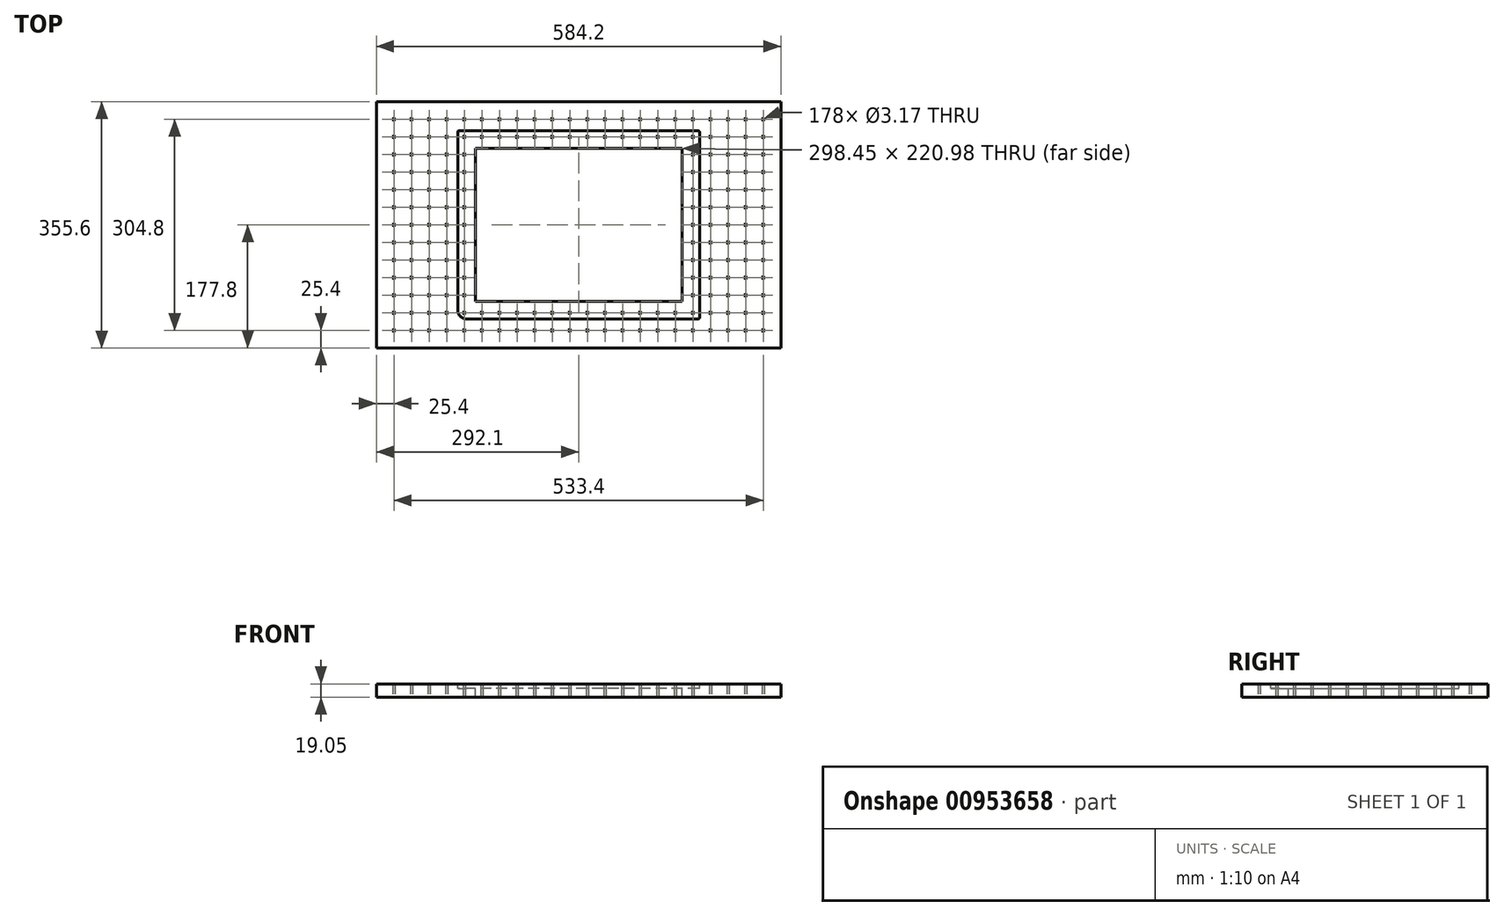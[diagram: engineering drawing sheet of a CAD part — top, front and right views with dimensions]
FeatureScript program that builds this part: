
annotation { "Feature Type Name" : "Feature", "Feature Type Description" : "" }
export const myFeature = defineFeature(function(context is Context, id is Id, definition is map)
    precondition{}
    {
        {
            var Q0;
            Q0=qCreatedBy(makeId("Top.planeOp"),FACE);
            var sketch = newSketch(context, id + "F0", { "sketchPlane" : qUnion([Q0])});
            skLineSegment(sketch, "E0.bottom", {"start": v(292.1, -177.8) * mm, "end": v(-292.1, -177.8) * mm});
            skLineSegment(sketch, "E0.top", {"start": v(292.1, 177.8) * mm, "end": v(-292.1, 177.8) * mm});
            skLineSegment(sketch, "E0.left", {"start": v(292.1, -177.8) * mm, "end": v(292.1, 177.8) * mm});
            skLineSegment(sketch, "E0.right", {"start": v(-292.1, -177.8) * mm, "end": v(-292.1, 177.8) * mm});
            skLineSegment(sketch, "E1", {"start": v(-292.1, -177.8) * mm, "end": v(-292.1, -152.4) * mm, "construction": true});
            skLineSegment(sketch, "E2", {"start": v(-292.1, -152.4) * mm, "end": v(-266.7, -152.4) * mm, "construction": true});
            skCircle(sketch, "E3", {"center": v(-266.7, -152.4) * mm, "radius": 1.59 * mm});
            skCircle(sketch, "E4.0.1.0", {"center": v(-266.7, -127) * mm, "radius": 1.59 * mm});
            skCircle(sketch, "E4.0.2.0", {"center": v(-266.7, -101.6) * mm, "radius": 1.59 * mm});
            skCircle(sketch, "E4.0.3.0", {"center": v(-266.7, -76.2) * mm, "radius": 1.59 * mm});
            skCircle(sketch, "E4.0.4.0", {"center": v(-266.7, -50.8) * mm, "radius": 1.59 * mm});
            skCircle(sketch, "E4.0.5.0", {"center": v(-266.7, -25.4) * mm, "radius": 1.59 * mm});
            skCircle(sketch, "E4.0.6.0", {"center": v(-266.7, 0) * mm, "radius": 1.59 * mm});
            skCircle(sketch, "E4.0.7.0", {"center": v(-266.7, 25.4) * mm, "radius": 1.59 * mm});
            skCircle(sketch, "E4.0.8.0", {"center": v(-266.7, 50.8) * mm, "radius": 1.59 * mm});
            skCircle(sketch, "E4.0.9.0", {"center": v(-266.7, 76.2) * mm, "radius": 1.59 * mm});
            skCircle(sketch, "E4.0.10.0", {"center": v(-266.7, 101.6) * mm, "radius": 1.59 * mm});
            skCircle(sketch, "E4.0.11.0", {"center": v(-266.7, 127) * mm, "radius": 1.59 * mm});
            skCircle(sketch, "E4.0.12.0", {"center": v(-266.7, 152.4) * mm, "radius": 1.59 * mm});
            skCircle(sketch, "E4.1.0.0", {"center": v(-241.3, -152.4) * mm, "radius": 1.59 * mm});
            skCircle(sketch, "E4.1.1.0", {"center": v(-241.3, -127) * mm, "radius": 1.59 * mm});
            skCircle(sketch, "E4.1.2.0", {"center": v(-241.3, -101.6) * mm, "radius": 1.59 * mm});
            skCircle(sketch, "E4.1.3.0", {"center": v(-241.3, -76.2) * mm, "radius": 1.59 * mm});
            skCircle(sketch, "E4.1.4.0", {"center": v(-241.3, -50.8) * mm, "radius": 1.59 * mm});
            skCircle(sketch, "E4.1.5.0", {"center": v(-241.3, -25.4) * mm, "radius": 1.59 * mm});
            skCircle(sketch, "E4.1.6.0", {"center": v(-241.3, 0) * mm, "radius": 1.59 * mm});
            skCircle(sketch, "E4.1.7.0", {"center": v(-241.3, 25.4) * mm, "radius": 1.59 * mm});
            skCircle(sketch, "E4.1.8.0", {"center": v(-241.3, 50.8) * mm, "radius": 1.59 * mm});
            skCircle(sketch, "E4.1.9.0", {"center": v(-241.3, 76.2) * mm, "radius": 1.59 * mm});
            skCircle(sketch, "E4.1.10.0", {"center": v(-241.3, 101.6) * mm, "radius": 1.59 * mm});
            skCircle(sketch, "E4.1.11.0", {"center": v(-241.3, 127) * mm, "radius": 1.59 * mm});
            skCircle(sketch, "E4.1.12.0", {"center": v(-241.3, 152.4) * mm, "radius": 1.59 * mm});
            skCircle(sketch, "E4.2.0.0", {"center": v(-215.9, -152.4) * mm, "radius": 1.59 * mm});
            skCircle(sketch, "E4.2.1.0", {"center": v(-215.9, -127) * mm, "radius": 1.59 * mm});
            skCircle(sketch, "E4.2.2.0", {"center": v(-215.9, -101.6) * mm, "radius": 1.59 * mm});
            skCircle(sketch, "E4.2.3.0", {"center": v(-215.9, -76.2) * mm, "radius": 1.59 * mm});
            skCircle(sketch, "E4.2.4.0", {"center": v(-215.9, -50.8) * mm, "radius": 1.59 * mm});
            skCircle(sketch, "E4.2.5.0", {"center": v(-215.9, -25.4) * mm, "radius": 1.59 * mm});
            skCircle(sketch, "E4.2.6.0", {"center": v(-215.9, 0) * mm, "radius": 1.59 * mm});
            skCircle(sketch, "E4.2.7.0", {"center": v(-215.9, 25.4) * mm, "radius": 1.59 * mm});
            skCircle(sketch, "E4.2.8.0", {"center": v(-215.9, 50.8) * mm, "radius": 1.59 * mm});
            skCircle(sketch, "E4.2.9.0", {"center": v(-215.9, 76.2) * mm, "radius": 1.59 * mm});
            skCircle(sketch, "E4.2.10.0", {"center": v(-215.9, 101.6) * mm, "radius": 1.59 * mm});
            skCircle(sketch, "E4.2.11.0", {"center": v(-215.9, 127) * mm, "radius": 1.59 * mm});
            skCircle(sketch, "E4.2.12.0", {"center": v(-215.9, 152.4) * mm, "radius": 1.59 * mm});
            skCircle(sketch, "E4.3.0.0", {"center": v(-190.5, -152.4) * mm, "radius": 1.59 * mm});
            skCircle(sketch, "E4.3.1.0", {"center": v(-190.5, -127) * mm, "radius": 1.59 * mm});
            skCircle(sketch, "E4.3.2.0", {"center": v(-190.5, -101.6) * mm, "radius": 1.59 * mm});
            skCircle(sketch, "E4.3.3.0", {"center": v(-190.5, -76.2) * mm, "radius": 1.59 * mm});
            skCircle(sketch, "E4.3.4.0", {"center": v(-190.5, -50.8) * mm, "radius": 1.59 * mm});
            skCircle(sketch, "E4.3.5.0", {"center": v(-190.5, -25.4) * mm, "radius": 1.59 * mm});
            skCircle(sketch, "E4.3.6.0", {"center": v(-190.5, 0) * mm, "radius": 1.59 * mm});
            skCircle(sketch, "E4.3.7.0", {"center": v(-190.5, 25.4) * mm, "radius": 1.59 * mm});
            skCircle(sketch, "E4.3.8.0", {"center": v(-190.5, 50.8) * mm, "radius": 1.59 * mm});
            skCircle(sketch, "E4.3.9.0", {"center": v(-190.5, 76.2) * mm, "radius": 1.59 * mm});
            skCircle(sketch, "E4.3.10.0", {"center": v(-190.5, 101.6) * mm, "radius": 1.59 * mm});
            skCircle(sketch, "E4.3.11.0", {"center": v(-190.5, 127) * mm, "radius": 1.59 * mm});
            skCircle(sketch, "E4.3.12.0", {"center": v(-190.5, 152.4) * mm, "radius": 1.59 * mm});
            skCircle(sketch, "E4.4.0.0", {"center": v(-165.1, -152.4) * mm, "radius": 1.59 * mm});
            skCircle(sketch, "E4.4.1.0", {"center": v(-165.1, -127) * mm, "radius": 1.59 * mm});
            skCircle(sketch, "E4.4.2.0", {"center": v(-165.1, -101.6) * mm, "radius": 1.59 * mm});
            skCircle(sketch, "E4.4.3.0", {"center": v(-165.1, -76.2) * mm, "radius": 1.59 * mm});
            skCircle(sketch, "E4.4.4.0", {"center": v(-165.1, -50.8) * mm, "radius": 1.59 * mm});
            skCircle(sketch, "E4.4.5.0", {"center": v(-165.1, -25.4) * mm, "radius": 1.59 * mm});
            skCircle(sketch, "E4.4.6.0", {"center": v(-165.1, 0) * mm, "radius": 1.59 * mm});
            skCircle(sketch, "E4.4.7.0", {"center": v(-165.1, 25.4) * mm, "radius": 1.59 * mm});
            skCircle(sketch, "E4.4.8.0", {"center": v(-165.1, 50.8) * mm, "radius": 1.59 * mm});
            skCircle(sketch, "E4.4.9.0", {"center": v(-165.1, 76.2) * mm, "radius": 1.59 * mm});
            skCircle(sketch, "E4.4.10.0", {"center": v(-165.1, 101.6) * mm, "radius": 1.59 * mm});
            skCircle(sketch, "E4.4.11.0", {"center": v(-165.1, 127) * mm, "radius": 1.59 * mm});
            skCircle(sketch, "E4.4.12.0", {"center": v(-165.1, 152.4) * mm, "radius": 1.59 * mm});
            skCircle(sketch, "E4.5.0.0", {"center": v(-139.7, -152.4) * mm, "radius": 1.59 * mm});
            skCircle(sketch, "E4.5.1.0", {"center": v(-139.7, -127) * mm, "radius": 1.59 * mm});
            skCircle(sketch, "E4.5.2.0", {"center": v(-139.7, -101.6) * mm, "radius": 1.59 * mm});
            skCircle(sketch, "E4.5.3.0", {"center": v(-139.7, -76.2) * mm, "radius": 1.59 * mm});
            skCircle(sketch, "E4.5.4.0", {"center": v(-139.7, -50.8) * mm, "radius": 1.59 * mm});
            skCircle(sketch, "E4.5.5.0", {"center": v(-139.7, -25.4) * mm, "radius": 1.59 * mm});
            skCircle(sketch, "E4.5.6.0", {"center": v(-139.7, 0) * mm, "radius": 1.59 * mm});
            skCircle(sketch, "E4.5.7.0", {"center": v(-139.7, 25.4) * mm, "radius": 1.59 * mm});
            skCircle(sketch, "E4.5.8.0", {"center": v(-139.7, 50.8) * mm, "radius": 1.59 * mm});
            skCircle(sketch, "E4.5.9.0", {"center": v(-139.7, 76.2) * mm, "radius": 1.59 * mm});
            skCircle(sketch, "E4.5.10.0", {"center": v(-139.7, 101.6) * mm, "radius": 1.59 * mm});
            skCircle(sketch, "E4.5.11.0", {"center": v(-139.7, 127) * mm, "radius": 1.59 * mm});
            skCircle(sketch, "E4.5.12.0", {"center": v(-139.7, 152.4) * mm, "radius": 1.59 * mm});
            skCircle(sketch, "E4.6.0.0", {"center": v(-114.3, -152.4) * mm, "radius": 1.59 * mm});
            skCircle(sketch, "E4.6.1.0", {"center": v(-114.3, -127) * mm, "radius": 1.59 * mm});
            skCircle(sketch, "E4.6.2.0", {"center": v(-114.3, -101.6) * mm, "radius": 1.59 * mm});
            skCircle(sketch, "E4.6.3.0", {"center": v(-114.3, -76.2) * mm, "radius": 1.59 * mm});
            skCircle(sketch, "E4.6.4.0", {"center": v(-114.3, -50.8) * mm, "radius": 1.59 * mm});
            skCircle(sketch, "E4.6.5.0", {"center": v(-114.3, -25.4) * mm, "radius": 1.59 * mm});
            skCircle(sketch, "E4.6.6.0", {"center": v(-114.3, 0) * mm, "radius": 1.59 * mm});
            skCircle(sketch, "E4.6.7.0", {"center": v(-114.3, 25.4) * mm, "radius": 1.59 * mm});
            skCircle(sketch, "E4.6.8.0", {"center": v(-114.3, 50.8) * mm, "radius": 1.59 * mm});
            skCircle(sketch, "E4.6.9.0", {"center": v(-114.3, 76.2) * mm, "radius": 1.59 * mm});
            skCircle(sketch, "E4.6.10.0", {"center": v(-114.3, 101.6) * mm, "radius": 1.59 * mm});
            skCircle(sketch, "E4.6.11.0", {"center": v(-114.3, 127) * mm, "radius": 1.59 * mm});
            skCircle(sketch, "E4.6.12.0", {"center": v(-114.3, 152.4) * mm, "radius": 1.59 * mm});
            skCircle(sketch, "E4.7.0.0", {"center": v(-88.9, -152.4) * mm, "radius": 1.59 * mm});
            skCircle(sketch, "E4.7.1.0", {"center": v(-88.9, -127) * mm, "radius": 1.59 * mm});
            skCircle(sketch, "E4.7.2.0", {"center": v(-88.9, -101.6) * mm, "radius": 1.59 * mm});
            skCircle(sketch, "E4.7.3.0", {"center": v(-88.9, -76.2) * mm, "radius": 1.59 * mm});
            skCircle(sketch, "E4.7.4.0", {"center": v(-88.9, -50.8) * mm, "radius": 1.59 * mm});
            skCircle(sketch, "E4.7.5.0", {"center": v(-88.9, -25.4) * mm, "radius": 1.59 * mm});
            skCircle(sketch, "E4.7.6.0", {"center": v(-88.9, 0) * mm, "radius": 1.59 * mm});
            skCircle(sketch, "E4.7.7.0", {"center": v(-88.9, 25.4) * mm, "radius": 1.59 * mm});
            skCircle(sketch, "E4.7.8.0", {"center": v(-88.9, 50.8) * mm, "radius": 1.59 * mm});
            skCircle(sketch, "E4.7.9.0", {"center": v(-88.9, 76.2) * mm, "radius": 1.59 * mm});
            skCircle(sketch, "E4.7.10.0", {"center": v(-88.9, 101.6) * mm, "radius": 1.59 * mm});
            skCircle(sketch, "E4.7.11.0", {"center": v(-88.9, 127) * mm, "radius": 1.59 * mm});
            skCircle(sketch, "E4.7.12.0", {"center": v(-88.9, 152.4) * mm, "radius": 1.59 * mm});
            skCircle(sketch, "E4.8.0.0", {"center": v(-63.5, -152.4) * mm, "radius": 1.59 * mm});
            skCircle(sketch, "E4.8.1.0", {"center": v(-63.5, -127) * mm, "radius": 1.59 * mm});
            skCircle(sketch, "E4.8.2.0", {"center": v(-63.5, -101.6) * mm, "radius": 1.59 * mm});
            skCircle(sketch, "E4.8.3.0", {"center": v(-63.5, -76.2) * mm, "radius": 1.59 * mm});
            skCircle(sketch, "E4.8.4.0", {"center": v(-63.5, -50.8) * mm, "radius": 1.59 * mm});
            skCircle(sketch, "E4.8.5.0", {"center": v(-63.5, -25.4) * mm, "radius": 1.59 * mm});
            skCircle(sketch, "E4.8.6.0", {"center": v(-63.5, 0) * mm, "radius": 1.59 * mm});
            skCircle(sketch, "E4.8.7.0", {"center": v(-63.5, 25.4) * mm, "radius": 1.59 * mm});
            skCircle(sketch, "E4.8.8.0", {"center": v(-63.5, 50.8) * mm, "radius": 1.59 * mm});
            skCircle(sketch, "E4.8.9.0", {"center": v(-63.5, 76.2) * mm, "radius": 1.59 * mm});
            skCircle(sketch, "E4.8.10.0", {"center": v(-63.5, 101.6) * mm, "radius": 1.59 * mm});
            skCircle(sketch, "E4.8.11.0", {"center": v(-63.5, 127) * mm, "radius": 1.59 * mm});
            skCircle(sketch, "E4.8.12.0", {"center": v(-63.5, 152.4) * mm, "radius": 1.59 * mm});
            skCircle(sketch, "E4.9.0.0", {"center": v(-38.1, -152.4) * mm, "radius": 1.59 * mm});
            skCircle(sketch, "E4.9.1.0", {"center": v(-38.1, -127) * mm, "radius": 1.59 * mm});
            skCircle(sketch, "E4.9.2.0", {"center": v(-38.1, -101.6) * mm, "radius": 1.59 * mm});
            skCircle(sketch, "E4.9.3.0", {"center": v(-38.1, -76.2) * mm, "radius": 1.59 * mm});
            skCircle(sketch, "E4.9.4.0", {"center": v(-38.1, -50.8) * mm, "radius": 1.59 * mm});
            skCircle(sketch, "E4.9.5.0", {"center": v(-38.1, -25.4) * mm, "radius": 1.59 * mm});
            skCircle(sketch, "E4.9.6.0", {"center": v(-38.1, 0) * mm, "radius": 1.59 * mm});
            skCircle(sketch, "E4.9.7.0", {"center": v(-38.1, 25.4) * mm, "radius": 1.59 * mm});
            skCircle(sketch, "E4.9.8.0", {"center": v(-38.1, 50.8) * mm, "radius": 1.59 * mm});
            skCircle(sketch, "E4.9.9.0", {"center": v(-38.1, 76.2) * mm, "radius": 1.59 * mm});
            skCircle(sketch, "E4.9.10.0", {"center": v(-38.1, 101.6) * mm, "radius": 1.59 * mm});
            skCircle(sketch, "E4.9.11.0", {"center": v(-38.1, 127) * mm, "radius": 1.59 * mm});
            skCircle(sketch, "E4.9.12.0", {"center": v(-38.1, 152.4) * mm, "radius": 1.59 * mm});
            skCircle(sketch, "E4.10.0.0", {"center": v(-12.7, -152.4) * mm, "radius": 1.59 * mm});
            skCircle(sketch, "E4.10.1.0", {"center": v(-12.7, -127) * mm, "radius": 1.59 * mm});
            skCircle(sketch, "E4.10.2.0", {"center": v(-12.7, -101.6) * mm, "radius": 1.59 * mm});
            skCircle(sketch, "E4.10.3.0", {"center": v(-12.7, -76.2) * mm, "radius": 1.59 * mm});
            skCircle(sketch, "E4.10.4.0", {"center": v(-12.7, -50.8) * mm, "radius": 1.59 * mm});
            skCircle(sketch, "E4.10.5.0", {"center": v(-12.7, -25.4) * mm, "radius": 1.59 * mm});
            skCircle(sketch, "E4.10.6.0", {"center": v(-12.7, 0) * mm, "radius": 1.59 * mm});
            skCircle(sketch, "E4.10.7.0", {"center": v(-12.7, 25.4) * mm, "radius": 1.59 * mm});
            skCircle(sketch, "E4.10.8.0", {"center": v(-12.7, 50.8) * mm, "radius": 1.59 * mm});
            skCircle(sketch, "E4.10.9.0", {"center": v(-12.7, 76.2) * mm, "radius": 1.59 * mm});
            skCircle(sketch, "E4.10.10.0", {"center": v(-12.7, 101.6) * mm, "radius": 1.59 * mm});
            skCircle(sketch, "E4.10.11.0", {"center": v(-12.7, 127) * mm, "radius": 1.59 * mm});
            skCircle(sketch, "E4.10.12.0", {"center": v(-12.7, 152.4) * mm, "radius": 1.59 * mm});
            skCircle(sketch, "E4.11.0.0", {"center": v(12.7, -152.4) * mm, "radius": 1.59 * mm});
            skCircle(sketch, "E4.11.1.0", {"center": v(12.7, -127) * mm, "radius": 1.59 * mm});
            skCircle(sketch, "E4.11.2.0", {"center": v(12.7, -101.6) * mm, "radius": 1.59 * mm});
            skCircle(sketch, "E4.11.3.0", {"center": v(12.7, -76.2) * mm, "radius": 1.59 * mm});
            skCircle(sketch, "E4.11.4.0", {"center": v(12.7, -50.8) * mm, "radius": 1.59 * mm});
            skCircle(sketch, "E4.11.5.0", {"center": v(12.7, -25.4) * mm, "radius": 1.59 * mm});
            skCircle(sketch, "E4.11.6.0", {"center": v(12.7, 0) * mm, "radius": 1.59 * mm});
            skCircle(sketch, "E4.11.7.0", {"center": v(12.7, 25.4) * mm, "radius": 1.59 * mm});
            skCircle(sketch, "E4.11.8.0", {"center": v(12.7, 50.8) * mm, "radius": 1.59 * mm});
            skCircle(sketch, "E4.11.9.0", {"center": v(12.7, 76.2) * mm, "radius": 1.59 * mm});
            skCircle(sketch, "E4.11.10.0", {"center": v(12.7, 101.6) * mm, "radius": 1.59 * mm});
            skCircle(sketch, "E4.11.11.0", {"center": v(12.7, 127) * mm, "radius": 1.59 * mm});
            skCircle(sketch, "E4.11.12.0", {"center": v(12.7, 152.4) * mm, "radius": 1.59 * mm});
            skCircle(sketch, "E4.12.0.0", {"center": v(38.1, -152.4) * mm, "radius": 1.59 * mm});
            skCircle(sketch, "E4.12.1.0", {"center": v(38.1, -127) * mm, "radius": 1.59 * mm});
            skCircle(sketch, "E4.12.2.0", {"center": v(38.1, -101.6) * mm, "radius": 1.59 * mm});
            skCircle(sketch, "E4.12.3.0", {"center": v(38.1, -76.2) * mm, "radius": 1.59 * mm});
            skCircle(sketch, "E4.12.4.0", {"center": v(38.1, -50.8) * mm, "radius": 1.59 * mm});
            skCircle(sketch, "E4.12.5.0", {"center": v(38.1, -25.4) * mm, "radius": 1.59 * mm});
            skCircle(sketch, "E4.12.6.0", {"center": v(38.1, 0) * mm, "radius": 1.59 * mm});
            skCircle(sketch, "E4.12.7.0", {"center": v(38.1, 25.4) * mm, "radius": 1.59 * mm});
            skCircle(sketch, "E4.12.8.0", {"center": v(38.1, 50.8) * mm, "radius": 1.59 * mm});
            skCircle(sketch, "E4.12.9.0", {"center": v(38.1, 76.2) * mm, "radius": 1.59 * mm});
            skCircle(sketch, "E4.12.10.0", {"center": v(38.1, 101.6) * mm, "radius": 1.59 * mm});
            skCircle(sketch, "E4.12.11.0", {"center": v(38.1, 127) * mm, "radius": 1.59 * mm});
            skCircle(sketch, "E4.12.12.0", {"center": v(38.1, 152.4) * mm, "radius": 1.59 * mm});
            skCircle(sketch, "E4.13.0.0", {"center": v(63.5, -152.4) * mm, "radius": 1.59 * mm});
            skCircle(sketch, "E4.13.1.0", {"center": v(63.5, -127) * mm, "radius": 1.59 * mm});
            skCircle(sketch, "E4.13.2.0", {"center": v(63.5, -101.6) * mm, "radius": 1.59 * mm});
            skCircle(sketch, "E4.13.3.0", {"center": v(63.5, -76.2) * mm, "radius": 1.59 * mm});
            skCircle(sketch, "E4.13.4.0", {"center": v(63.5, -50.8) * mm, "radius": 1.59 * mm});
            skCircle(sketch, "E4.13.5.0", {"center": v(63.5, -25.4) * mm, "radius": 1.59 * mm});
            skCircle(sketch, "E4.13.6.0", {"center": v(63.5, 0) * mm, "radius": 1.59 * mm});
            skCircle(sketch, "E4.13.7.0", {"center": v(63.5, 25.4) * mm, "radius": 1.59 * mm});
            skCircle(sketch, "E4.13.8.0", {"center": v(63.5, 50.8) * mm, "radius": 1.59 * mm});
            skCircle(sketch, "E4.13.9.0", {"center": v(63.5, 76.2) * mm, "radius": 1.59 * mm});
            skCircle(sketch, "E4.13.10.0", {"center": v(63.5, 101.6) * mm, "radius": 1.59 * mm});
            skCircle(sketch, "E4.13.11.0", {"center": v(63.5, 127) * mm, "radius": 1.59 * mm});
            skCircle(sketch, "E4.13.12.0", {"center": v(63.5, 152.4) * mm, "radius": 1.59 * mm});
            skCircle(sketch, "E4.14.0.0", {"center": v(88.9, -152.4) * mm, "radius": 1.59 * mm});
            skCircle(sketch, "E4.14.1.0", {"center": v(88.9, -127) * mm, "radius": 1.59 * mm});
            skCircle(sketch, "E4.14.2.0", {"center": v(88.9, -101.6) * mm, "radius": 1.59 * mm});
            skCircle(sketch, "E4.14.3.0", {"center": v(88.9, -76.2) * mm, "radius": 1.59 * mm});
            skCircle(sketch, "E4.14.4.0", {"center": v(88.9, -50.8) * mm, "radius": 1.59 * mm});
            skCircle(sketch, "E4.14.5.0", {"center": v(88.9, -25.4) * mm, "radius": 1.59 * mm});
            skCircle(sketch, "E4.14.6.0", {"center": v(88.9, 0) * mm, "radius": 1.59 * mm});
            skCircle(sketch, "E4.14.7.0", {"center": v(88.9, 25.4) * mm, "radius": 1.59 * mm});
            skCircle(sketch, "E4.14.8.0", {"center": v(88.9, 50.8) * mm, "radius": 1.59 * mm});
            skCircle(sketch, "E4.14.9.0", {"center": v(88.9, 76.2) * mm, "radius": 1.59 * mm});
            skCircle(sketch, "E4.14.10.0", {"center": v(88.9, 101.6) * mm, "radius": 1.59 * mm});
            skCircle(sketch, "E4.14.11.0", {"center": v(88.9, 127) * mm, "radius": 1.59 * mm});
            skCircle(sketch, "E4.14.12.0", {"center": v(88.9, 152.4) * mm, "radius": 1.59 * mm});
            skCircle(sketch, "E4.15.0.0", {"center": v(114.3, -152.4) * mm, "radius": 1.59 * mm});
            skCircle(sketch, "E4.15.1.0", {"center": v(114.3, -127) * mm, "radius": 1.59 * mm});
            skCircle(sketch, "E4.15.2.0", {"center": v(114.3, -101.6) * mm, "radius": 1.59 * mm});
            skCircle(sketch, "E4.15.3.0", {"center": v(114.3, -76.2) * mm, "radius": 1.59 * mm});
            skCircle(sketch, "E4.15.4.0", {"center": v(114.3, -50.8) * mm, "radius": 1.59 * mm});
            skCircle(sketch, "E4.15.5.0", {"center": v(114.3, -25.4) * mm, "radius": 1.59 * mm});
            skCircle(sketch, "E4.15.6.0", {"center": v(114.3, 0) * mm, "radius": 1.59 * mm});
            skCircle(sketch, "E4.15.7.0", {"center": v(114.3, 25.4) * mm, "radius": 1.59 * mm});
            skCircle(sketch, "E4.15.8.0", {"center": v(114.3, 50.8) * mm, "radius": 1.59 * mm});
            skCircle(sketch, "E4.15.9.0", {"center": v(114.3, 76.2) * mm, "radius": 1.59 * mm});
            skCircle(sketch, "E4.15.10.0", {"center": v(114.3, 101.6) * mm, "radius": 1.59 * mm});
            skCircle(sketch, "E4.15.11.0", {"center": v(114.3, 127) * mm, "radius": 1.59 * mm});
            skCircle(sketch, "E4.15.12.0", {"center": v(114.3, 152.4) * mm, "radius": 1.59 * mm});
            skCircle(sketch, "E4.16.0.0", {"center": v(139.7, -152.4) * mm, "radius": 1.59 * mm});
            skCircle(sketch, "E4.16.1.0", {"center": v(139.7, -127) * mm, "radius": 1.59 * mm});
            skCircle(sketch, "E4.16.2.0", {"center": v(139.7, -101.6) * mm, "radius": 1.59 * mm});
            skCircle(sketch, "E4.16.3.0", {"center": v(139.7, -76.2) * mm, "radius": 1.59 * mm});
            skCircle(sketch, "E4.16.4.0", {"center": v(139.7, -50.8) * mm, "radius": 1.59 * mm});
            skCircle(sketch, "E4.16.5.0", {"center": v(139.7, -25.4) * mm, "radius": 1.59 * mm});
            skCircle(sketch, "E4.16.6.0", {"center": v(139.7, 0) * mm, "radius": 1.59 * mm});
            skCircle(sketch, "E4.16.7.0", {"center": v(139.7, 25.4) * mm, "radius": 1.59 * mm});
            skCircle(sketch, "E4.16.8.0", {"center": v(139.7, 50.8) * mm, "radius": 1.59 * mm});
            skCircle(sketch, "E4.16.9.0", {"center": v(139.7, 76.2) * mm, "radius": 1.59 * mm});
            skCircle(sketch, "E4.16.10.0", {"center": v(139.7, 101.6) * mm, "radius": 1.59 * mm});
            skCircle(sketch, "E4.16.11.0", {"center": v(139.7, 127) * mm, "radius": 1.59 * mm});
            skCircle(sketch, "E4.16.12.0", {"center": v(139.7, 152.4) * mm, "radius": 1.59 * mm});
            skCircle(sketch, "E4.17.0.0", {"center": v(165.1, -152.4) * mm, "radius": 1.59 * mm});
            skCircle(sketch, "E4.17.1.0", {"center": v(165.1, -127) * mm, "radius": 1.59 * mm});
            skCircle(sketch, "E4.17.2.0", {"center": v(165.1, -101.6) * mm, "radius": 1.59 * mm});
            skCircle(sketch, "E4.17.3.0", {"center": v(165.1, -76.2) * mm, "radius": 1.59 * mm});
            skCircle(sketch, "E4.17.4.0", {"center": v(165.1, -50.8) * mm, "radius": 1.59 * mm});
            skCircle(sketch, "E4.17.5.0", {"center": v(165.1, -25.4) * mm, "radius": 1.59 * mm});
            skCircle(sketch, "E4.17.6.0", {"center": v(165.1, 0) * mm, "radius": 1.59 * mm});
            skCircle(sketch, "E4.17.7.0", {"center": v(165.1, 25.4) * mm, "radius": 1.59 * mm});
            skCircle(sketch, "E4.17.8.0", {"center": v(165.1, 50.8) * mm, "radius": 1.59 * mm});
            skCircle(sketch, "E4.17.9.0", {"center": v(165.1, 76.2) * mm, "radius": 1.59 * mm});
            skCircle(sketch, "E4.17.10.0", {"center": v(165.1, 101.6) * mm, "radius": 1.59 * mm});
            skCircle(sketch, "E4.17.11.0", {"center": v(165.1, 127) * mm, "radius": 1.59 * mm});
            skCircle(sketch, "E4.17.12.0", {"center": v(165.1, 152.4) * mm, "radius": 1.59 * mm});
            skCircle(sketch, "E4.18.0.0", {"center": v(190.5, -152.4) * mm, "radius": 1.59 * mm});
            skCircle(sketch, "E4.18.1.0", {"center": v(190.5, -127) * mm, "radius": 1.59 * mm});
            skCircle(sketch, "E4.18.2.0", {"center": v(190.5, -101.6) * mm, "radius": 1.59 * mm});
            skCircle(sketch, "E4.18.3.0", {"center": v(190.5, -76.2) * mm, "radius": 1.59 * mm});
            skCircle(sketch, "E4.18.4.0", {"center": v(190.5, -50.8) * mm, "radius": 1.59 * mm});
            skCircle(sketch, "E4.18.5.0", {"center": v(190.5, -25.4) * mm, "radius": 1.59 * mm});
            skCircle(sketch, "E4.18.6.0", {"center": v(190.5, 0) * mm, "radius": 1.59 * mm});
            skCircle(sketch, "E4.18.7.0", {"center": v(190.5, 25.4) * mm, "radius": 1.59 * mm});
            skCircle(sketch, "E4.18.8.0", {"center": v(190.5, 50.8) * mm, "radius": 1.59 * mm});
            skCircle(sketch, "E4.18.9.0", {"center": v(190.5, 76.2) * mm, "radius": 1.59 * mm});
            skCircle(sketch, "E4.18.10.0", {"center": v(190.5, 101.6) * mm, "radius": 1.59 * mm});
            skCircle(sketch, "E4.18.11.0", {"center": v(190.5, 127) * mm, "radius": 1.59 * mm});
            skCircle(sketch, "E4.18.12.0", {"center": v(190.5, 152.4) * mm, "radius": 1.59 * mm});
            skCircle(sketch, "E4.19.0.0", {"center": v(215.9, -152.4) * mm, "radius": 1.59 * mm});
            skCircle(sketch, "E4.19.1.0", {"center": v(215.9, -127) * mm, "radius": 1.59 * mm});
            skCircle(sketch, "E4.19.2.0", {"center": v(215.9, -101.6) * mm, "radius": 1.59 * mm});
            skCircle(sketch, "E4.19.3.0", {"center": v(215.9, -76.2) * mm, "radius": 1.59 * mm});
            skCircle(sketch, "E4.19.4.0", {"center": v(215.9, -50.8) * mm, "radius": 1.59 * mm});
            skCircle(sketch, "E4.19.5.0", {"center": v(215.9, -25.4) * mm, "radius": 1.59 * mm});
            skCircle(sketch, "E4.19.6.0", {"center": v(215.9, 0) * mm, "radius": 1.59 * mm});
            skCircle(sketch, "E4.19.7.0", {"center": v(215.9, 25.4) * mm, "radius": 1.59 * mm});
            skCircle(sketch, "E4.19.8.0", {"center": v(215.9, 50.8) * mm, "radius": 1.59 * mm});
            skCircle(sketch, "E4.19.9.0", {"center": v(215.9, 76.2) * mm, "radius": 1.59 * mm});
            skCircle(sketch, "E4.19.10.0", {"center": v(215.9, 101.6) * mm, "radius": 1.59 * mm});
            skCircle(sketch, "E4.19.11.0", {"center": v(215.9, 127) * mm, "radius": 1.59 * mm});
            skCircle(sketch, "E4.19.12.0", {"center": v(215.9, 152.4) * mm, "radius": 1.59 * mm});
            skCircle(sketch, "E4.20.0.0", {"center": v(241.3, -152.4) * mm, "radius": 1.59 * mm});
            skCircle(sketch, "E4.20.1.0", {"center": v(241.3, -127) * mm, "radius": 1.59 * mm});
            skCircle(sketch, "E4.20.2.0", {"center": v(241.3, -101.6) * mm, "radius": 1.59 * mm});
            skCircle(sketch, "E4.20.3.0", {"center": v(241.3, -76.2) * mm, "radius": 1.59 * mm});
            skCircle(sketch, "E4.20.4.0", {"center": v(241.3, -50.8) * mm, "radius": 1.59 * mm});
            skCircle(sketch, "E4.20.5.0", {"center": v(241.3, -25.4) * mm, "radius": 1.59 * mm});
            skCircle(sketch, "E4.20.6.0", {"center": v(241.3, 0) * mm, "radius": 1.59 * mm});
            skCircle(sketch, "E4.20.7.0", {"center": v(241.3, 25.4) * mm, "radius": 1.59 * mm});
            skCircle(sketch, "E4.20.8.0", {"center": v(241.3, 50.8) * mm, "radius": 1.59 * mm});
            skCircle(sketch, "E4.20.9.0", {"center": v(241.3, 76.2) * mm, "radius": 1.59 * mm});
            skCircle(sketch, "E4.20.10.0", {"center": v(241.3, 101.6) * mm, "radius": 1.59 * mm});
            skCircle(sketch, "E4.20.11.0", {"center": v(241.3, 127) * mm, "radius": 1.59 * mm});
            skCircle(sketch, "E4.20.12.0", {"center": v(241.3, 152.4) * mm, "radius": 1.59 * mm});
            skCircle(sketch, "E4.21.0.0", {"center": v(266.7, -152.4) * mm, "radius": 1.59 * mm});
            skCircle(sketch, "E4.21.1.0", {"center": v(266.7, -127) * mm, "radius": 1.59 * mm});
            skCircle(sketch, "E4.21.2.0", {"center": v(266.7, -101.6) * mm, "radius": 1.59 * mm});
            skCircle(sketch, "E4.21.3.0", {"center": v(266.7, -76.2) * mm, "radius": 1.59 * mm});
            skCircle(sketch, "E4.21.4.0", {"center": v(266.7, -50.8) * mm, "radius": 1.59 * mm});
            skCircle(sketch, "E4.21.5.0", {"center": v(266.7, -25.4) * mm, "radius": 1.59 * mm});
            skCircle(sketch, "E4.21.6.0", {"center": v(266.7, 0) * mm, "radius": 1.59 * mm});
            skCircle(sketch, "E4.21.7.0", {"center": v(266.7, 25.4) * mm, "radius": 1.59 * mm});
            skCircle(sketch, "E4.21.8.0", {"center": v(266.7, 50.8) * mm, "radius": 1.59 * mm});
            skCircle(sketch, "E4.21.9.0", {"center": v(266.7, 76.2) * mm, "radius": 1.59 * mm});
            skCircle(sketch, "E4.21.10.0", {"center": v(266.7, 101.6) * mm, "radius": 1.59 * mm});
            skCircle(sketch, "E4.21.11.0", {"center": v(266.7, 127) * mm, "radius": 1.59 * mm});
            skCircle(sketch, "E4.21.12.0", {"center": v(266.7, 152.4) * mm, "radius": 1.59 * mm});
            skLineSegment(sketch, "E4.direction1", {"start": v(-266.7, -152.4) * mm, "end": v(-241.3, -152.4) * mm, "construction": true});
            skLineSegment(sketch, "E4.direction2", {"start": v(-266.7, -152.4) * mm, "end": v(-266.7, -127) * mm, "construction": true});
            skSolve(sketch);
        }
        {
            var Q0;
            Q0=makeQuery(id+"F0.imprint","IMPRINT",FACE,{"disambiguationData":[TD([[makeQuery(id+"F0.imprint","IMPRINT",EDGE,{"derivedFrom":sQuery(id+"F0.wireOp",EDGE,"E0.bottom")}),-1.0]])]});
            extrude(context, id + "F1", {"entities" : qUnion([Q0]), "depth" : 19.05 * mm, "offsetDistance" : 25.4 * mm});
        }
        {
            var Q0;
            Q0=makeQuery(id+"F1.opExtrude","CAP_FACE",FACE,{"disambiguationData":[OSD([sQuery(id+"F0.wireOp",EDGE,"W0l0qKWO-XmLI-oeky-ciGQ-aFYPakqgF4cn"),sQuery(id+"F0.wireOp",EDGE,"4a86b1cf-17ad-482d-8b79-44e54a63ab70.0.1.0"),sQuery(id+"F0.wireOp",EDGE,"4a86b1cf-17ad-482d-8b79-44e54a63ab70.0.2.0"),sQuery(id+"F0.wireOp",EDGE,"4a86b1cf-17ad-482d-8b79-44e54a63ab70.0.3.0"),sQuery(id+"F0.wireOp",EDGE,"4a86b1cf-17ad-482d-8b79-44e54a63ab70.0.4.0"),sQuery(id+"F0.wireOp",EDGE,"4a86b1cf-17ad-482d-8b79-44e54a63ab70.0.5.0"),sQuery(id+"F0.wireOp",EDGE,"4a86b1cf-17ad-482d-8b79-44e54a63ab70.0.6.0"),sQuery(id+"F0.wireOp",EDGE,"4a86b1cf-17ad-482d-8b79-44e54a63ab70.0.7.0"),sQuery(id+"F0.wireOp",EDGE,"4a86b1cf-17ad-482d-8b79-44e54a63ab70.0.8.0"),sQuery(id+"F0.wireOp",EDGE,"4a86b1cf-17ad-482d-8b79-44e54a63ab70.0.9.0"),sQuery(id+"F0.wireOp",EDGE,"4a86b1cf-17ad-482d-8b79-44e54a63ab70.0.10.0"),sQuery(id+"F0.wireOp",EDGE,"4a86b1cf-17ad-482d-8b79-44e54a63ab70.0.11.0"),sQuery(id+"F0.wireOp",EDGE,"4a86b1cf-17ad-482d-8b79-44e54a63ab70.0.12.0"),sQuery(id+"F0.wireOp",EDGE,"4a86b1cf-17ad-482d-8b79-44e54a63ab70.1.0.0"),sQuery(id+"F0.wireOp",EDGE,"4a86b1cf-17ad-482d-8b79-44e54a63ab70.1.1.0"),sQuery(id+"F0.wireOp",EDGE,"4a86b1cf-17ad-482d-8b79-44e54a63ab70.1.2.0"),sQuery(id+"F0.wireOp",EDGE,"4a86b1cf-17ad-482d-8b79-44e54a63ab70.1.3.0"),sQuery(id+"F0.wireOp",EDGE,"4a86b1cf-17ad-482d-8b79-44e54a63ab70.1.4.0"),sQuery(id+"F0.wireOp",EDGE,"4a86b1cf-17ad-482d-8b79-44e54a63ab70.1.5.0"),sQuery(id+"F0.wireOp",EDGE,"4a86b1cf-17ad-482d-8b79-44e54a63ab70.1.6.0"),sQuery(id+"F0.wireOp",EDGE,"4a86b1cf-17ad-482d-8b79-44e54a63ab70.1.7.0"),sQuery(id+"F0.wireOp",EDGE,"4a86b1cf-17ad-482d-8b79-44e54a63ab70.1.8.0"),sQuery(id+"F0.wireOp",EDGE,"4a86b1cf-17ad-482d-8b79-44e54a63ab70.1.9.0"),sQuery(id+"F0.wireOp",EDGE,"4a86b1cf-17ad-482d-8b79-44e54a63ab70.1.10.0"),sQuery(id+"F0.wireOp",EDGE,"4a86b1cf-17ad-482d-8b79-44e54a63ab70.1.11.0"),sQuery(id+"F0.wireOp",EDGE,"4a86b1cf-17ad-482d-8b79-44e54a63ab70.1.12.0"),sQuery(id+"F0.wireOp",EDGE,"4a86b1cf-17ad-482d-8b79-44e54a63ab70.2.0.0"),sQuery(id+"F0.wireOp",EDGE,"4a86b1cf-17ad-482d-8b79-44e54a63ab70.2.1.0"),sQuery(id+"F0.wireOp",EDGE,"4a86b1cf-17ad-482d-8b79-44e54a63ab70.2.2.0"),sQuery(id+"F0.wireOp",EDGE,"4a86b1cf-17ad-482d-8b79-44e54a63ab70.2.3.0"),sQuery(id+"F0.wireOp",EDGE,"4a86b1cf-17ad-482d-8b79-44e54a63ab70.2.4.0"),sQuery(id+"F0.wireOp",EDGE,"4a86b1cf-17ad-482d-8b79-44e54a63ab70.2.5.0"),sQuery(id+"F0.wireOp",EDGE,"4a86b1cf-17ad-482d-8b79-44e54a63ab70.2.6.0"),sQuery(id+"F0.wireOp",EDGE,"4a86b1cf-17ad-482d-8b79-44e54a63ab70.2.7.0"),sQuery(id+"F0.wireOp",EDGE,"4a86b1cf-17ad-482d-8b79-44e54a63ab70.2.8.0"),sQuery(id+"F0.wireOp",EDGE,"4a86b1cf-17ad-482d-8b79-44e54a63ab70.2.9.0"),sQuery(id+"F0.wireOp",EDGE,"4a86b1cf-17ad-482d-8b79-44e54a63ab70.2.10.0"),sQuery(id+"F0.wireOp",EDGE,"4a86b1cf-17ad-482d-8b79-44e54a63ab70.2.11.0"),sQuery(id+"F0.wireOp",EDGE,"4a86b1cf-17ad-482d-8b79-44e54a63ab70.2.12.0"),sQuery(id+"F0.wireOp",EDGE,"4a86b1cf-17ad-482d-8b79-44e54a63ab70.3.0.0"),sQuery(id+"F0.wireOp",EDGE,"4a86b1cf-17ad-482d-8b79-44e54a63ab70.3.1.0"),sQuery(id+"F0.wireOp",EDGE,"4a86b1cf-17ad-482d-8b79-44e54a63ab70.3.2.0"),sQuery(id+"F0.wireOp",EDGE,"4a86b1cf-17ad-482d-8b79-44e54a63ab70.3.3.0"),sQuery(id+"F0.wireOp",EDGE,"4a86b1cf-17ad-482d-8b79-44e54a63ab70.3.4.0"),sQuery(id+"F0.wireOp",EDGE,"4a86b1cf-17ad-482d-8b79-44e54a63ab70.3.5.0"),sQuery(id+"F0.wireOp",EDGE,"4a86b1cf-17ad-482d-8b79-44e54a63ab70.3.6.0"),sQuery(id+"F0.wireOp",EDGE,"4a86b1cf-17ad-482d-8b79-44e54a63ab70.3.7.0"),sQuery(id+"F0.wireOp",EDGE,"4a86b1cf-17ad-482d-8b79-44e54a63ab70.3.8.0"),sQuery(id+"F0.wireOp",EDGE,"4a86b1cf-17ad-482d-8b79-44e54a63ab70.3.9.0"),sQuery(id+"F0.wireOp",EDGE,"4a86b1cf-17ad-482d-8b79-44e54a63ab70.3.10.0"),sQuery(id+"F0.wireOp",EDGE,"4a86b1cf-17ad-482d-8b79-44e54a63ab70.3.11.0"),sQuery(id+"F0.wireOp",EDGE,"4a86b1cf-17ad-482d-8b79-44e54a63ab70.3.12.0"),sQuery(id+"F0.wireOp",EDGE,"4a86b1cf-17ad-482d-8b79-44e54a63ab70.4.0.0"),sQuery(id+"F0.wireOp",EDGE,"4a86b1cf-17ad-482d-8b79-44e54a63ab70.4.1.0"),sQuery(id+"F0.wireOp",EDGE,"4a86b1cf-17ad-482d-8b79-44e54a63ab70.4.2.0"),sQuery(id+"F0.wireOp",EDGE,"4a86b1cf-17ad-482d-8b79-44e54a63ab70.4.3.0"),sQuery(id+"F0.wireOp",EDGE,"4a86b1cf-17ad-482d-8b79-44e54a63ab70.4.4.0"),sQuery(id+"F0.wireOp",EDGE,"4a86b1cf-17ad-482d-8b79-44e54a63ab70.4.5.0"),sQuery(id+"F0.wireOp",EDGE,"4a86b1cf-17ad-482d-8b79-44e54a63ab70.4.6.0"),sQuery(id+"F0.wireOp",EDGE,"4a86b1cf-17ad-482d-8b79-44e54a63ab70.4.7.0"),sQuery(id+"F0.wireOp",EDGE,"4a86b1cf-17ad-482d-8b79-44e54a63ab70.4.8.0"),sQuery(id+"F0.wireOp",EDGE,"4a86b1cf-17ad-482d-8b79-44e54a63ab70.4.9.0"),sQuery(id+"F0.wireOp",EDGE,"4a86b1cf-17ad-482d-8b79-44e54a63ab70.4.10.0"),sQuery(id+"F0.wireOp",EDGE,"4a86b1cf-17ad-482d-8b79-44e54a63ab70.4.11.0"),sQuery(id+"F0.wireOp",EDGE,"4a86b1cf-17ad-482d-8b79-44e54a63ab70.4.12.0"),sQuery(id+"F0.wireOp",EDGE,"4a86b1cf-17ad-482d-8b79-44e54a63ab70.5.0.0"),sQuery(id+"F0.wireOp",EDGE,"4a86b1cf-17ad-482d-8b79-44e54a63ab70.5.1.0"),sQuery(id+"F0.wireOp",EDGE,"4a86b1cf-17ad-482d-8b79-44e54a63ab70.5.2.0"),sQuery(id+"F0.wireOp",EDGE,"4a86b1cf-17ad-482d-8b79-44e54a63ab70.5.3.0"),sQuery(id+"F0.wireOp",EDGE,"4a86b1cf-17ad-482d-8b79-44e54a63ab70.5.4.0"),sQuery(id+"F0.wireOp",EDGE,"4a86b1cf-17ad-482d-8b79-44e54a63ab70.5.5.0"),sQuery(id+"F0.wireOp",EDGE,"4a86b1cf-17ad-482d-8b79-44e54a63ab70.5.6.0"),sQuery(id+"F0.wireOp",EDGE,"4a86b1cf-17ad-482d-8b79-44e54a63ab70.5.7.0"),sQuery(id+"F0.wireOp",EDGE,"4a86b1cf-17ad-482d-8b79-44e54a63ab70.5.8.0"),sQuery(id+"F0.wireOp",EDGE,"4a86b1cf-17ad-482d-8b79-44e54a63ab70.5.9.0"),sQuery(id+"F0.wireOp",EDGE,"4a86b1cf-17ad-482d-8b79-44e54a63ab70.5.10.0"),sQuery(id+"F0.wireOp",EDGE,"4a86b1cf-17ad-482d-8b79-44e54a63ab70.5.11.0"),sQuery(id+"F0.wireOp",EDGE,"4a86b1cf-17ad-482d-8b79-44e54a63ab70.5.12.0"),sQuery(id+"F0.wireOp",EDGE,"4a86b1cf-17ad-482d-8b79-44e54a63ab70.6.0.0"),sQuery(id+"F0.wireOp",EDGE,"4a86b1cf-17ad-482d-8b79-44e54a63ab70.6.1.0"),sQuery(id+"F0.wireOp",EDGE,"4a86b1cf-17ad-482d-8b79-44e54a63ab70.6.2.0"),sQuery(id+"F0.wireOp",EDGE,"4a86b1cf-17ad-482d-8b79-44e54a63ab70.6.3.0"),sQuery(id+"F0.wireOp",EDGE,"4a86b1cf-17ad-482d-8b79-44e54a63ab70.6.4.0"),sQuery(id+"F0.wireOp",EDGE,"4a86b1cf-17ad-482d-8b79-44e54a63ab70.6.5.0"),sQuery(id+"F0.wireOp",EDGE,"4a86b1cf-17ad-482d-8b79-44e54a63ab70.6.6.0"),sQuery(id+"F0.wireOp",EDGE,"4a86b1cf-17ad-482d-8b79-44e54a63ab70.6.7.0"),sQuery(id+"F0.wireOp",EDGE,"4a86b1cf-17ad-482d-8b79-44e54a63ab70.6.8.0"),sQuery(id+"F0.wireOp",EDGE,"4a86b1cf-17ad-482d-8b79-44e54a63ab70.6.9.0"),sQuery(id+"F0.wireOp",EDGE,"4a86b1cf-17ad-482d-8b79-44e54a63ab70.6.10.0"),sQuery(id+"F0.wireOp",EDGE,"4a86b1cf-17ad-482d-8b79-44e54a63ab70.6.11.0"),sQuery(id+"F0.wireOp",EDGE,"4a86b1cf-17ad-482d-8b79-44e54a63ab70.6.12.0"),sQuery(id+"F0.wireOp",EDGE,"4a86b1cf-17ad-482d-8b79-44e54a63ab70.7.0.0"),sQuery(id+"F0.wireOp",EDGE,"4a86b1cf-17ad-482d-8b79-44e54a63ab70.7.1.0"),sQuery(id+"F0.wireOp",EDGE,"4a86b1cf-17ad-482d-8b79-44e54a63ab70.7.2.0"),sQuery(id+"F0.wireOp",EDGE,"4a86b1cf-17ad-482d-8b79-44e54a63ab70.7.3.0"),sQuery(id+"F0.wireOp",EDGE,"4a86b1cf-17ad-482d-8b79-44e54a63ab70.7.4.0"),sQuery(id+"F0.wireOp",EDGE,"4a86b1cf-17ad-482d-8b79-44e54a63ab70.7.5.0"),sQuery(id+"F0.wireOp",EDGE,"4a86b1cf-17ad-482d-8b79-44e54a63ab70.7.6.0"),sQuery(id+"F0.wireOp",EDGE,"4a86b1cf-17ad-482d-8b79-44e54a63ab70.7.7.0"),sQuery(id+"F0.wireOp",EDGE,"4a86b1cf-17ad-482d-8b79-44e54a63ab70.7.8.0"),sQuery(id+"F0.wireOp",EDGE,"4a86b1cf-17ad-482d-8b79-44e54a63ab70.7.9.0"),sQuery(id+"F0.wireOp",EDGE,"4a86b1cf-17ad-482d-8b79-44e54a63ab70.7.10.0"),sQuery(id+"F0.wireOp",EDGE,"4a86b1cf-17ad-482d-8b79-44e54a63ab70.7.11.0"),sQuery(id+"F0.wireOp",EDGE,"4a86b1cf-17ad-482d-8b79-44e54a63ab70.7.12.0"),sQuery(id+"F0.wireOp",EDGE,"4a86b1cf-17ad-482d-8b79-44e54a63ab70.8.0.0"),sQuery(id+"F0.wireOp",EDGE,"4a86b1cf-17ad-482d-8b79-44e54a63ab70.8.1.0"),sQuery(id+"F0.wireOp",EDGE,"4a86b1cf-17ad-482d-8b79-44e54a63ab70.8.2.0"),sQuery(id+"F0.wireOp",EDGE,"4a86b1cf-17ad-482d-8b79-44e54a63ab70.8.3.0"),sQuery(id+"F0.wireOp",EDGE,"4a86b1cf-17ad-482d-8b79-44e54a63ab70.8.4.0"),sQuery(id+"F0.wireOp",EDGE,"4a86b1cf-17ad-482d-8b79-44e54a63ab70.8.5.0"),sQuery(id+"F0.wireOp",EDGE,"4a86b1cf-17ad-482d-8b79-44e54a63ab70.8.6.0"),sQuery(id+"F0.wireOp",EDGE,"4a86b1cf-17ad-482d-8b79-44e54a63ab70.8.7.0"),sQuery(id+"F0.wireOp",EDGE,"4a86b1cf-17ad-482d-8b79-44e54a63ab70.8.8.0"),sQuery(id+"F0.wireOp",EDGE,"4a86b1cf-17ad-482d-8b79-44e54a63ab70.8.9.0"),sQuery(id+"F0.wireOp",EDGE,"4a86b1cf-17ad-482d-8b79-44e54a63ab70.8.10.0"),sQuery(id+"F0.wireOp",EDGE,"4a86b1cf-17ad-482d-8b79-44e54a63ab70.8.11.0"),sQuery(id+"F0.wireOp",EDGE,"4a86b1cf-17ad-482d-8b79-44e54a63ab70.8.12.0"),sQuery(id+"F0.wireOp",EDGE,"4a86b1cf-17ad-482d-8b79-44e54a63ab70.9.0.0"),sQuery(id+"F0.wireOp",EDGE,"4a86b1cf-17ad-482d-8b79-44e54a63ab70.9.1.0"),sQuery(id+"F0.wireOp",EDGE,"4a86b1cf-17ad-482d-8b79-44e54a63ab70.9.2.0"),sQuery(id+"F0.wireOp",EDGE,"4a86b1cf-17ad-482d-8b79-44e54a63ab70.9.3.0"),sQuery(id+"F0.wireOp",EDGE,"4a86b1cf-17ad-482d-8b79-44e54a63ab70.9.4.0"),sQuery(id+"F0.wireOp",EDGE,"4a86b1cf-17ad-482d-8b79-44e54a63ab70.9.5.0"),sQuery(id+"F0.wireOp",EDGE,"4a86b1cf-17ad-482d-8b79-44e54a63ab70.9.6.0"),sQuery(id+"F0.wireOp",EDGE,"4a86b1cf-17ad-482d-8b79-44e54a63ab70.9.7.0"),sQuery(id+"F0.wireOp",EDGE,"4a86b1cf-17ad-482d-8b79-44e54a63ab70.9.8.0"),sQuery(id+"F0.wireOp",EDGE,"4a86b1cf-17ad-482d-8b79-44e54a63ab70.9.9.0"),sQuery(id+"F0.wireOp",EDGE,"4a86b1cf-17ad-482d-8b79-44e54a63ab70.9.10.0"),sQuery(id+"F0.wireOp",EDGE,"4a86b1cf-17ad-482d-8b79-44e54a63ab70.9.11.0"),sQuery(id+"F0.wireOp",EDGE,"4a86b1cf-17ad-482d-8b79-44e54a63ab70.9.12.0"),sQuery(id+"F0.wireOp",EDGE,"4a86b1cf-17ad-482d-8b79-44e54a63ab70.10.0.0"),sQuery(id+"F0.wireOp",EDGE,"4a86b1cf-17ad-482d-8b79-44e54a63ab70.10.1.0"),sQuery(id+"F0.wireOp",EDGE,"4a86b1cf-17ad-482d-8b79-44e54a63ab70.10.2.0"),sQuery(id+"F0.wireOp",EDGE,"4a86b1cf-17ad-482d-8b79-44e54a63ab70.10.3.0"),sQuery(id+"F0.wireOp",EDGE,"4a86b1cf-17ad-482d-8b79-44e54a63ab70.10.4.0"),sQuery(id+"F0.wireOp",EDGE,"4a86b1cf-17ad-482d-8b79-44e54a63ab70.10.5.0"),sQuery(id+"F0.wireOp",EDGE,"4a86b1cf-17ad-482d-8b79-44e54a63ab70.10.6.0"),sQuery(id+"F0.wireOp",EDGE,"4a86b1cf-17ad-482d-8b79-44e54a63ab70.10.7.0"),sQuery(id+"F0.wireOp",EDGE,"4a86b1cf-17ad-482d-8b79-44e54a63ab70.10.8.0"),sQuery(id+"F0.wireOp",EDGE,"4a86b1cf-17ad-482d-8b79-44e54a63ab70.10.9.0"),sQuery(id+"F0.wireOp",EDGE,"4a86b1cf-17ad-482d-8b79-44e54a63ab70.10.10.0"),sQuery(id+"F0.wireOp",EDGE,"4a86b1cf-17ad-482d-8b79-44e54a63ab70.10.11.0"),sQuery(id+"F0.wireOp",EDGE,"4a86b1cf-17ad-482d-8b79-44e54a63ab70.10.12.0"),sQuery(id+"F0.wireOp",EDGE,"4a86b1cf-17ad-482d-8b79-44e54a63ab70.11.0.0"),sQuery(id+"F0.wireOp",EDGE,"4a86b1cf-17ad-482d-8b79-44e54a63ab70.11.1.0"),sQuery(id+"F0.wireOp",EDGE,"4a86b1cf-17ad-482d-8b79-44e54a63ab70.11.2.0"),sQuery(id+"F0.wireOp",EDGE,"4a86b1cf-17ad-482d-8b79-44e54a63ab70.11.3.0"),sQuery(id+"F0.wireOp",EDGE,"4a86b1cf-17ad-482d-8b79-44e54a63ab70.11.4.0"),sQuery(id+"F0.wireOp",EDGE,"4a86b1cf-17ad-482d-8b79-44e54a63ab70.11.5.0"),sQuery(id+"F0.wireOp",EDGE,"4a86b1cf-17ad-482d-8b79-44e54a63ab70.11.6.0"),sQuery(id+"F0.wireOp",EDGE,"4a86b1cf-17ad-482d-8b79-44e54a63ab70.11.7.0"),sQuery(id+"F0.wireOp",EDGE,"4a86b1cf-17ad-482d-8b79-44e54a63ab70.11.8.0"),sQuery(id+"F0.wireOp",EDGE,"4a86b1cf-17ad-482d-8b79-44e54a63ab70.11.9.0"),sQuery(id+"F0.wireOp",EDGE,"4a86b1cf-17ad-482d-8b79-44e54a63ab70.11.10.0"),sQuery(id+"F0.wireOp",EDGE,"4a86b1cf-17ad-482d-8b79-44e54a63ab70.11.11.0"),sQuery(id+"F0.wireOp",EDGE,"4a86b1cf-17ad-482d-8b79-44e54a63ab70.11.12.0"),sQuery(id+"F0.wireOp",EDGE,"4a86b1cf-17ad-482d-8b79-44e54a63ab70.12.0.0"),sQuery(id+"F0.wireOp",EDGE,"4a86b1cf-17ad-482d-8b79-44e54a63ab70.12.1.0"),sQuery(id+"F0.wireOp",EDGE,"4a86b1cf-17ad-482d-8b79-44e54a63ab70.12.2.0"),sQuery(id+"F0.wireOp",EDGE,"4a86b1cf-17ad-482d-8b79-44e54a63ab70.12.3.0"),sQuery(id+"F0.wireOp",EDGE,"4a86b1cf-17ad-482d-8b79-44e54a63ab70.12.4.0"),sQuery(id+"F0.wireOp",EDGE,"4a86b1cf-17ad-482d-8b79-44e54a63ab70.12.5.0"),sQuery(id+"F0.wireOp",EDGE,"4a86b1cf-17ad-482d-8b79-44e54a63ab70.12.6.0"),sQuery(id+"F0.wireOp",EDGE,"4a86b1cf-17ad-482d-8b79-44e54a63ab70.12.7.0"),sQuery(id+"F0.wireOp",EDGE,"4a86b1cf-17ad-482d-8b79-44e54a63ab70.12.8.0"),sQuery(id+"F0.wireOp",EDGE,"4a86b1cf-17ad-482d-8b79-44e54a63ab70.12.9.0"),sQuery(id+"F0.wireOp",EDGE,"4a86b1cf-17ad-482d-8b79-44e54a63ab70.12.10.0"),sQuery(id+"F0.wireOp",EDGE,"4a86b1cf-17ad-482d-8b79-44e54a63ab70.12.11.0"),sQuery(id+"F0.wireOp",EDGE,"4a86b1cf-17ad-482d-8b79-44e54a63ab70.12.12.0"),sQuery(id+"F0.wireOp",EDGE,"4a86b1cf-17ad-482d-8b79-44e54a63ab70.13.0.0"),sQuery(id+"F0.wireOp",EDGE,"4a86b1cf-17ad-482d-8b79-44e54a63ab70.13.1.0"),sQuery(id+"F0.wireOp",EDGE,"4a86b1cf-17ad-482d-8b79-44e54a63ab70.13.2.0"),sQuery(id+"F0.wireOp",EDGE,"4a86b1cf-17ad-482d-8b79-44e54a63ab70.13.3.0"),sQuery(id+"F0.wireOp",EDGE,"4a86b1cf-17ad-482d-8b79-44e54a63ab70.13.4.0"),sQuery(id+"F0.wireOp",EDGE,"4a86b1cf-17ad-482d-8b79-44e54a63ab70.13.5.0"),sQuery(id+"F0.wireOp",EDGE,"4a86b1cf-17ad-482d-8b79-44e54a63ab70.13.6.0"),sQuery(id+"F0.wireOp",EDGE,"4a86b1cf-17ad-482d-8b79-44e54a63ab70.13.7.0"),sQuery(id+"F0.wireOp",EDGE,"4a86b1cf-17ad-482d-8b79-44e54a63ab70.13.8.0"),sQuery(id+"F0.wireOp",EDGE,"4a86b1cf-17ad-482d-8b79-44e54a63ab70.13.9.0"),sQuery(id+"F0.wireOp",EDGE,"4a86b1cf-17ad-482d-8b79-44e54a63ab70.13.10.0"),sQuery(id+"F0.wireOp",EDGE,"4a86b1cf-17ad-482d-8b79-44e54a63ab70.13.11.0"),sQuery(id+"F0.wireOp",EDGE,"4a86b1cf-17ad-482d-8b79-44e54a63ab70.13.12.0"),sQuery(id+"F0.wireOp",EDGE,"4a86b1cf-17ad-482d-8b79-44e54a63ab70.14.0.0"),sQuery(id+"F0.wireOp",EDGE,"4a86b1cf-17ad-482d-8b79-44e54a63ab70.14.1.0"),sQuery(id+"F0.wireOp",EDGE,"4a86b1cf-17ad-482d-8b79-44e54a63ab70.14.2.0"),sQuery(id+"F0.wireOp",EDGE,"4a86b1cf-17ad-482d-8b79-44e54a63ab70.14.3.0"),sQuery(id+"F0.wireOp",EDGE,"4a86b1cf-17ad-482d-8b79-44e54a63ab70.14.4.0"),sQuery(id+"F0.wireOp",EDGE,"4a86b1cf-17ad-482d-8b79-44e54a63ab70.14.5.0"),sQuery(id+"F0.wireOp",EDGE,"4a86b1cf-17ad-482d-8b79-44e54a63ab70.14.6.0"),sQuery(id+"F0.wireOp",EDGE,"4a86b1cf-17ad-482d-8b79-44e54a63ab70.14.7.0"),sQuery(id+"F0.wireOp",EDGE,"4a86b1cf-17ad-482d-8b79-44e54a63ab70.14.8.0"),sQuery(id+"F0.wireOp",EDGE,"4a86b1cf-17ad-482d-8b79-44e54a63ab70.14.9.0"),sQuery(id+"F0.wireOp",EDGE,"4a86b1cf-17ad-482d-8b79-44e54a63ab70.14.10.0"),sQuery(id+"F0.wireOp",EDGE,"4a86b1cf-17ad-482d-8b79-44e54a63ab70.14.11.0"),sQuery(id+"F0.wireOp",EDGE,"4a86b1cf-17ad-482d-8b79-44e54a63ab70.14.12.0"),sQuery(id+"F0.wireOp",EDGE,"4a86b1cf-17ad-482d-8b79-44e54a63ab70.15.0.0"),sQuery(id+"F0.wireOp",EDGE,"4a86b1cf-17ad-482d-8b79-44e54a63ab70.15.1.0"),sQuery(id+"F0.wireOp",EDGE,"4a86b1cf-17ad-482d-8b79-44e54a63ab70.15.2.0"),sQuery(id+"F0.wireOp",EDGE,"4a86b1cf-17ad-482d-8b79-44e54a63ab70.15.3.0"),sQuery(id+"F0.wireOp",EDGE,"4a86b1cf-17ad-482d-8b79-44e54a63ab70.15.4.0"),sQuery(id+"F0.wireOp",EDGE,"4a86b1cf-17ad-482d-8b79-44e54a63ab70.15.5.0"),sQuery(id+"F0.wireOp",EDGE,"4a86b1cf-17ad-482d-8b79-44e54a63ab70.15.6.0"),sQuery(id+"F0.wireOp",EDGE,"4a86b1cf-17ad-482d-8b79-44e54a63ab70.15.7.0"),sQuery(id+"F0.wireOp",EDGE,"4a86b1cf-17ad-482d-8b79-44e54a63ab70.15.8.0"),sQuery(id+"F0.wireOp",EDGE,"4a86b1cf-17ad-482d-8b79-44e54a63ab70.15.9.0"),sQuery(id+"F0.wireOp",EDGE,"4a86b1cf-17ad-482d-8b79-44e54a63ab70.15.10.0"),sQuery(id+"F0.wireOp",EDGE,"4a86b1cf-17ad-482d-8b79-44e54a63ab70.15.11.0"),sQuery(id+"F0.wireOp",EDGE,"4a86b1cf-17ad-482d-8b79-44e54a63ab70.15.12.0"),sQuery(id+"F0.wireOp",EDGE,"E0.bottom"),sQuery(id+"F0.wireOp",EDGE,"E0.top"),sQuery(id+"F0.wireOp",EDGE,"E0.left"),sQuery(id+"F0.wireOp",EDGE,"E0.right")])],"isStart":false});
            var sketch = newSketch(context, id + "F2", { "sketchPlane" : qUnion([Q0])});
            skLineSegment(sketch, "E5.bottom", {"start": v(173, -135.89) * mm, "end": v(-161.54, -135.9) * mm});
            skLineSegment(sketch, "E5.top", {"start": v(173, 135.9) * mm, "end": v(-173, 135.89) * mm});
            skLineSegment(sketch, "E5.left", {"start": v(174.63, -134.26) * mm, "end": v(174.63, 134.26) * mm});
            skLineSegment(sketch, "E5.right", {"start": v(-174.63, -122.8) * mm, "end": v(-174.63, 134.26) * mm});
            skPoint(sketch, "E5.middle", {"position": v(0, 0) * mm});
            skPoint(sketch, "E6.visualSharp", {"position": v(-174.63, 135.89) * mm});
            skArc(sketch, "E6.filletArc", {"start": v(-173, 135.89) * mm, "mid": v(-174.15, 135.41) * mm, "end": v(-174.63, 134.26) * mm});
            skPoint(sketch, "E7.visualSharp", {"position": v(174.63, 135.9) * mm});
            skArc(sketch, "E7.filletArc", {"start": v(174.63, 134.26) * mm, "mid": v(174.15, 135.41) * mm, "end": v(173, 135.9) * mm});
            skPoint(sketch, "E8.visualSharp", {"position": v(174.63, -135.89) * mm});
            skArc(sketch, "E8.filletArc", {"start": v(173, -135.89) * mm, "mid": v(174.15, -135.41) * mm, "end": v(174.63, -134.26) * mm});
            skPoint(sketch, "E9.visualSharp", {"position": v(-174.63, -135.9) * mm});
            skArc(sketch, "E9.filletArc", {"start": v(-174.63, -122.8) * mm, "mid": v(-170.8, -132.06) * mm, "end": v(-161.54, -135.9) * mm});
            skSolve(sketch);
        }
        {
            var Q0;
            Q0=makeQuery(id+"F2.imprint","IMPRINT",FACE,{"disambiguationData":[TD([[makeQuery(id+"F2.imprint","IMPRINT",EDGE,{"derivedFrom":sQuery(id+"F2.wireOp",EDGE,"E5.bottom")}),-1.0]])]});
            extrude(context, id + "F3", {"entities" : qUnion([Q0]), "operationType" : NewBodyOperationType.REMOVE, "oppositeDirection" : true, "depth" : 6.35 * mm, "offsetDistance" : 25.4 * mm});
        }
        {
            var Q0;
            Q0=makeQuery(id+"F3.boolean.opBoolean","COPY",FACE,{"derivedFrom":makeQuery(id+"F3.opExtrude","CAP_FACE",FACE,{"disambiguationData":[OSD([sQuery(id+"F0.wireOp",EDGE,"4a86b1cf-17ad-482d-8b79-44e54a63ab70.1.1.0"),sQuery(id+"F0.wireOp",EDGE,"4a86b1cf-17ad-482d-8b79-44e54a63ab70.1.2.0"),sQuery(id+"F0.wireOp",EDGE,"4a86b1cf-17ad-482d-8b79-44e54a63ab70.1.3.0"),sQuery(id+"F0.wireOp",EDGE,"4a86b1cf-17ad-482d-8b79-44e54a63ab70.1.4.0"),sQuery(id+"F0.wireOp",EDGE,"4a86b1cf-17ad-482d-8b79-44e54a63ab70.1.5.0"),sQuery(id+"F0.wireOp",EDGE,"4a86b1cf-17ad-482d-8b79-44e54a63ab70.1.6.0"),sQuery(id+"F0.wireOp",EDGE,"4a86b1cf-17ad-482d-8b79-44e54a63ab70.1.7.0"),sQuery(id+"F0.wireOp",EDGE,"4a86b1cf-17ad-482d-8b79-44e54a63ab70.1.8.0"),sQuery(id+"F0.wireOp",EDGE,"4a86b1cf-17ad-482d-8b79-44e54a63ab70.1.9.0"),sQuery(id+"F0.wireOp",EDGE,"4a86b1cf-17ad-482d-8b79-44e54a63ab70.1.10.0"),sQuery(id+"F0.wireOp",EDGE,"4a86b1cf-17ad-482d-8b79-44e54a63ab70.1.11.0"),sQuery(id+"F0.wireOp",EDGE,"4a86b1cf-17ad-482d-8b79-44e54a63ab70.2.1.0"),sQuery(id+"F0.wireOp",EDGE,"4a86b1cf-17ad-482d-8b79-44e54a63ab70.2.2.0"),sQuery(id+"F0.wireOp",EDGE,"4a86b1cf-17ad-482d-8b79-44e54a63ab70.2.3.0"),sQuery(id+"F0.wireOp",EDGE,"4a86b1cf-17ad-482d-8b79-44e54a63ab70.2.4.0"),sQuery(id+"F0.wireOp",EDGE,"4a86b1cf-17ad-482d-8b79-44e54a63ab70.2.5.0"),sQuery(id+"F0.wireOp",EDGE,"4a86b1cf-17ad-482d-8b79-44e54a63ab70.2.6.0"),sQuery(id+"F0.wireOp",EDGE,"4a86b1cf-17ad-482d-8b79-44e54a63ab70.2.7.0"),sQuery(id+"F0.wireOp",EDGE,"4a86b1cf-17ad-482d-8b79-44e54a63ab70.2.8.0"),sQuery(id+"F0.wireOp",EDGE,"4a86b1cf-17ad-482d-8b79-44e54a63ab70.2.9.0"),sQuery(id+"F0.wireOp",EDGE,"4a86b1cf-17ad-482d-8b79-44e54a63ab70.2.10.0"),sQuery(id+"F0.wireOp",EDGE,"4a86b1cf-17ad-482d-8b79-44e54a63ab70.2.11.0"),sQuery(id+"F0.wireOp",EDGE,"4a86b1cf-17ad-482d-8b79-44e54a63ab70.3.1.0"),sQuery(id+"F0.wireOp",EDGE,"4a86b1cf-17ad-482d-8b79-44e54a63ab70.3.2.0"),sQuery(id+"F0.wireOp",EDGE,"4a86b1cf-17ad-482d-8b79-44e54a63ab70.3.3.0"),sQuery(id+"F0.wireOp",EDGE,"4a86b1cf-17ad-482d-8b79-44e54a63ab70.3.4.0"),sQuery(id+"F0.wireOp",EDGE,"4a86b1cf-17ad-482d-8b79-44e54a63ab70.3.5.0"),sQuery(id+"F0.wireOp",EDGE,"4a86b1cf-17ad-482d-8b79-44e54a63ab70.3.6.0"),sQuery(id+"F0.wireOp",EDGE,"4a86b1cf-17ad-482d-8b79-44e54a63ab70.3.7.0"),sQuery(id+"F0.wireOp",EDGE,"4a86b1cf-17ad-482d-8b79-44e54a63ab70.3.8.0"),sQuery(id+"F0.wireOp",EDGE,"4a86b1cf-17ad-482d-8b79-44e54a63ab70.3.9.0"),sQuery(id+"F0.wireOp",EDGE,"4a86b1cf-17ad-482d-8b79-44e54a63ab70.3.10.0"),sQuery(id+"F0.wireOp",EDGE,"4a86b1cf-17ad-482d-8b79-44e54a63ab70.3.11.0"),sQuery(id+"F0.wireOp",EDGE,"4a86b1cf-17ad-482d-8b79-44e54a63ab70.4.1.0"),sQuery(id+"F0.wireOp",EDGE,"4a86b1cf-17ad-482d-8b79-44e54a63ab70.4.2.0"),sQuery(id+"F0.wireOp",EDGE,"4a86b1cf-17ad-482d-8b79-44e54a63ab70.4.3.0"),sQuery(id+"F0.wireOp",EDGE,"4a86b1cf-17ad-482d-8b79-44e54a63ab70.4.4.0"),sQuery(id+"F0.wireOp",EDGE,"4a86b1cf-17ad-482d-8b79-44e54a63ab70.4.5.0"),sQuery(id+"F0.wireOp",EDGE,"4a86b1cf-17ad-482d-8b79-44e54a63ab70.4.6.0"),sQuery(id+"F0.wireOp",EDGE,"4a86b1cf-17ad-482d-8b79-44e54a63ab70.4.7.0"),sQuery(id+"F0.wireOp",EDGE,"4a86b1cf-17ad-482d-8b79-44e54a63ab70.4.8.0"),sQuery(id+"F0.wireOp",EDGE,"4a86b1cf-17ad-482d-8b79-44e54a63ab70.4.9.0"),sQuery(id+"F0.wireOp",EDGE,"4a86b1cf-17ad-482d-8b79-44e54a63ab70.4.10.0"),sQuery(id+"F0.wireOp",EDGE,"4a86b1cf-17ad-482d-8b79-44e54a63ab70.4.11.0"),sQuery(id+"F0.wireOp",EDGE,"4a86b1cf-17ad-482d-8b79-44e54a63ab70.5.1.0"),sQuery(id+"F0.wireOp",EDGE,"4a86b1cf-17ad-482d-8b79-44e54a63ab70.5.2.0"),sQuery(id+"F0.wireOp",EDGE,"4a86b1cf-17ad-482d-8b79-44e54a63ab70.5.3.0"),sQuery(id+"F0.wireOp",EDGE,"4a86b1cf-17ad-482d-8b79-44e54a63ab70.5.4.0"),sQuery(id+"F0.wireOp",EDGE,"4a86b1cf-17ad-482d-8b79-44e54a63ab70.5.5.0"),sQuery(id+"F0.wireOp",EDGE,"4a86b1cf-17ad-482d-8b79-44e54a63ab70.5.6.0"),sQuery(id+"F0.wireOp",EDGE,"4a86b1cf-17ad-482d-8b79-44e54a63ab70.5.7.0"),sQuery(id+"F0.wireOp",EDGE,"4a86b1cf-17ad-482d-8b79-44e54a63ab70.5.8.0"),sQuery(id+"F0.wireOp",EDGE,"4a86b1cf-17ad-482d-8b79-44e54a63ab70.5.9.0"),sQuery(id+"F0.wireOp",EDGE,"4a86b1cf-17ad-482d-8b79-44e54a63ab70.5.10.0"),sQuery(id+"F0.wireOp",EDGE,"4a86b1cf-17ad-482d-8b79-44e54a63ab70.5.11.0"),sQuery(id+"F0.wireOp",EDGE,"4a86b1cf-17ad-482d-8b79-44e54a63ab70.6.1.0"),sQuery(id+"F0.wireOp",EDGE,"4a86b1cf-17ad-482d-8b79-44e54a63ab70.6.2.0"),sQuery(id+"F0.wireOp",EDGE,"4a86b1cf-17ad-482d-8b79-44e54a63ab70.6.3.0"),sQuery(id+"F0.wireOp",EDGE,"4a86b1cf-17ad-482d-8b79-44e54a63ab70.6.4.0"),sQuery(id+"F0.wireOp",EDGE,"4a86b1cf-17ad-482d-8b79-44e54a63ab70.6.5.0"),sQuery(id+"F0.wireOp",EDGE,"4a86b1cf-17ad-482d-8b79-44e54a63ab70.6.6.0"),sQuery(id+"F0.wireOp",EDGE,"4a86b1cf-17ad-482d-8b79-44e54a63ab70.6.7.0"),sQuery(id+"F0.wireOp",EDGE,"4a86b1cf-17ad-482d-8b79-44e54a63ab70.6.8.0"),sQuery(id+"F0.wireOp",EDGE,"4a86b1cf-17ad-482d-8b79-44e54a63ab70.6.9.0"),sQuery(id+"F0.wireOp",EDGE,"4a86b1cf-17ad-482d-8b79-44e54a63ab70.6.10.0"),sQuery(id+"F0.wireOp",EDGE,"4a86b1cf-17ad-482d-8b79-44e54a63ab70.6.11.0"),sQuery(id+"F0.wireOp",EDGE,"4a86b1cf-17ad-482d-8b79-44e54a63ab70.7.1.0"),sQuery(id+"F0.wireOp",EDGE,"4a86b1cf-17ad-482d-8b79-44e54a63ab70.7.2.0"),sQuery(id+"F0.wireOp",EDGE,"4a86b1cf-17ad-482d-8b79-44e54a63ab70.7.3.0"),sQuery(id+"F0.wireOp",EDGE,"4a86b1cf-17ad-482d-8b79-44e54a63ab70.7.4.0"),sQuery(id+"F0.wireOp",EDGE,"4a86b1cf-17ad-482d-8b79-44e54a63ab70.7.5.0"),sQuery(id+"F0.wireOp",EDGE,"4a86b1cf-17ad-482d-8b79-44e54a63ab70.7.6.0"),sQuery(id+"F0.wireOp",EDGE,"4a86b1cf-17ad-482d-8b79-44e54a63ab70.7.7.0"),sQuery(id+"F0.wireOp",EDGE,"4a86b1cf-17ad-482d-8b79-44e54a63ab70.7.8.0"),sQuery(id+"F0.wireOp",EDGE,"4a86b1cf-17ad-482d-8b79-44e54a63ab70.7.9.0"),sQuery(id+"F0.wireOp",EDGE,"4a86b1cf-17ad-482d-8b79-44e54a63ab70.7.10.0"),sQuery(id+"F0.wireOp",EDGE,"4a86b1cf-17ad-482d-8b79-44e54a63ab70.7.11.0"),sQuery(id+"F0.wireOp",EDGE,"4a86b1cf-17ad-482d-8b79-44e54a63ab70.8.1.0"),sQuery(id+"F0.wireOp",EDGE,"4a86b1cf-17ad-482d-8b79-44e54a63ab70.8.2.0"),sQuery(id+"F0.wireOp",EDGE,"4a86b1cf-17ad-482d-8b79-44e54a63ab70.8.3.0"),sQuery(id+"F0.wireOp",EDGE,"4a86b1cf-17ad-482d-8b79-44e54a63ab70.8.4.0"),sQuery(id+"F0.wireOp",EDGE,"4a86b1cf-17ad-482d-8b79-44e54a63ab70.8.5.0"),sQuery(id+"F0.wireOp",EDGE,"4a86b1cf-17ad-482d-8b79-44e54a63ab70.8.6.0"),sQuery(id+"F0.wireOp",EDGE,"4a86b1cf-17ad-482d-8b79-44e54a63ab70.8.7.0"),sQuery(id+"F0.wireOp",EDGE,"4a86b1cf-17ad-482d-8b79-44e54a63ab70.8.8.0"),sQuery(id+"F0.wireOp",EDGE,"4a86b1cf-17ad-482d-8b79-44e54a63ab70.8.9.0"),sQuery(id+"F0.wireOp",EDGE,"4a86b1cf-17ad-482d-8b79-44e54a63ab70.8.10.0"),sQuery(id+"F0.wireOp",EDGE,"4a86b1cf-17ad-482d-8b79-44e54a63ab70.8.11.0"),sQuery(id+"F0.wireOp",EDGE,"4a86b1cf-17ad-482d-8b79-44e54a63ab70.9.1.0"),sQuery(id+"F0.wireOp",EDGE,"4a86b1cf-17ad-482d-8b79-44e54a63ab70.9.2.0"),sQuery(id+"F0.wireOp",EDGE,"4a86b1cf-17ad-482d-8b79-44e54a63ab70.9.3.0"),sQuery(id+"F0.wireOp",EDGE,"4a86b1cf-17ad-482d-8b79-44e54a63ab70.9.4.0"),sQuery(id+"F0.wireOp",EDGE,"4a86b1cf-17ad-482d-8b79-44e54a63ab70.9.5.0"),sQuery(id+"F0.wireOp",EDGE,"4a86b1cf-17ad-482d-8b79-44e54a63ab70.9.6.0"),sQuery(id+"F0.wireOp",EDGE,"4a86b1cf-17ad-482d-8b79-44e54a63ab70.9.7.0"),sQuery(id+"F0.wireOp",EDGE,"4a86b1cf-17ad-482d-8b79-44e54a63ab70.9.8.0"),sQuery(id+"F0.wireOp",EDGE,"4a86b1cf-17ad-482d-8b79-44e54a63ab70.9.9.0"),sQuery(id+"F0.wireOp",EDGE,"4a86b1cf-17ad-482d-8b79-44e54a63ab70.9.10.0"),sQuery(id+"F0.wireOp",EDGE,"4a86b1cf-17ad-482d-8b79-44e54a63ab70.9.11.0"),sQuery(id+"F0.wireOp",EDGE,"4a86b1cf-17ad-482d-8b79-44e54a63ab70.10.1.0"),sQuery(id+"F0.wireOp",EDGE,"4a86b1cf-17ad-482d-8b79-44e54a63ab70.10.2.0"),sQuery(id+"F0.wireOp",EDGE,"4a86b1cf-17ad-482d-8b79-44e54a63ab70.10.3.0"),sQuery(id+"F0.wireOp",EDGE,"4a86b1cf-17ad-482d-8b79-44e54a63ab70.10.4.0"),sQuery(id+"F0.wireOp",EDGE,"4a86b1cf-17ad-482d-8b79-44e54a63ab70.10.5.0"),sQuery(id+"F0.wireOp",EDGE,"4a86b1cf-17ad-482d-8b79-44e54a63ab70.10.6.0"),sQuery(id+"F0.wireOp",EDGE,"4a86b1cf-17ad-482d-8b79-44e54a63ab70.10.7.0"),sQuery(id+"F0.wireOp",EDGE,"4a86b1cf-17ad-482d-8b79-44e54a63ab70.10.8.0"),sQuery(id+"F0.wireOp",EDGE,"4a86b1cf-17ad-482d-8b79-44e54a63ab70.10.9.0"),sQuery(id+"F0.wireOp",EDGE,"4a86b1cf-17ad-482d-8b79-44e54a63ab70.10.10.0"),sQuery(id+"F0.wireOp",EDGE,"4a86b1cf-17ad-482d-8b79-44e54a63ab70.10.11.0"),sQuery(id+"F0.wireOp",EDGE,"4a86b1cf-17ad-482d-8b79-44e54a63ab70.11.1.0"),sQuery(id+"F0.wireOp",EDGE,"4a86b1cf-17ad-482d-8b79-44e54a63ab70.11.2.0"),sQuery(id+"F0.wireOp",EDGE,"4a86b1cf-17ad-482d-8b79-44e54a63ab70.11.3.0"),sQuery(id+"F0.wireOp",EDGE,"4a86b1cf-17ad-482d-8b79-44e54a63ab70.11.4.0"),sQuery(id+"F0.wireOp",EDGE,"4a86b1cf-17ad-482d-8b79-44e54a63ab70.11.5.0"),sQuery(id+"F0.wireOp",EDGE,"4a86b1cf-17ad-482d-8b79-44e54a63ab70.11.6.0"),sQuery(id+"F0.wireOp",EDGE,"4a86b1cf-17ad-482d-8b79-44e54a63ab70.11.7.0"),sQuery(id+"F0.wireOp",EDGE,"4a86b1cf-17ad-482d-8b79-44e54a63ab70.11.8.0"),sQuery(id+"F0.wireOp",EDGE,"4a86b1cf-17ad-482d-8b79-44e54a63ab70.11.9.0"),sQuery(id+"F0.wireOp",EDGE,"4a86b1cf-17ad-482d-8b79-44e54a63ab70.11.10.0"),sQuery(id+"F0.wireOp",EDGE,"4a86b1cf-17ad-482d-8b79-44e54a63ab70.11.11.0"),sQuery(id+"F0.wireOp",EDGE,"4a86b1cf-17ad-482d-8b79-44e54a63ab70.12.1.0"),sQuery(id+"F0.wireOp",EDGE,"4a86b1cf-17ad-482d-8b79-44e54a63ab70.12.2.0"),sQuery(id+"F0.wireOp",EDGE,"4a86b1cf-17ad-482d-8b79-44e54a63ab70.12.3.0"),sQuery(id+"F0.wireOp",EDGE,"4a86b1cf-17ad-482d-8b79-44e54a63ab70.12.4.0"),sQuery(id+"F0.wireOp",EDGE,"4a86b1cf-17ad-482d-8b79-44e54a63ab70.12.5.0"),sQuery(id+"F0.wireOp",EDGE,"4a86b1cf-17ad-482d-8b79-44e54a63ab70.12.6.0"),sQuery(id+"F0.wireOp",EDGE,"4a86b1cf-17ad-482d-8b79-44e54a63ab70.12.7.0"),sQuery(id+"F0.wireOp",EDGE,"4a86b1cf-17ad-482d-8b79-44e54a63ab70.12.8.0"),sQuery(id+"F0.wireOp",EDGE,"4a86b1cf-17ad-482d-8b79-44e54a63ab70.12.9.0"),sQuery(id+"F0.wireOp",EDGE,"4a86b1cf-17ad-482d-8b79-44e54a63ab70.12.10.0"),sQuery(id+"F0.wireOp",EDGE,"4a86b1cf-17ad-482d-8b79-44e54a63ab70.12.11.0"),sQuery(id+"F0.wireOp",EDGE,"4a86b1cf-17ad-482d-8b79-44e54a63ab70.13.1.0"),sQuery(id+"F0.wireOp",EDGE,"4a86b1cf-17ad-482d-8b79-44e54a63ab70.13.2.0"),sQuery(id+"F0.wireOp",EDGE,"4a86b1cf-17ad-482d-8b79-44e54a63ab70.13.3.0"),sQuery(id+"F0.wireOp",EDGE,"4a86b1cf-17ad-482d-8b79-44e54a63ab70.13.4.0"),sQuery(id+"F0.wireOp",EDGE,"4a86b1cf-17ad-482d-8b79-44e54a63ab70.13.5.0"),sQuery(id+"F0.wireOp",EDGE,"4a86b1cf-17ad-482d-8b79-44e54a63ab70.13.6.0"),sQuery(id+"F0.wireOp",EDGE,"4a86b1cf-17ad-482d-8b79-44e54a63ab70.13.7.0"),sQuery(id+"F0.wireOp",EDGE,"4a86b1cf-17ad-482d-8b79-44e54a63ab70.13.8.0"),sQuery(id+"F0.wireOp",EDGE,"4a86b1cf-17ad-482d-8b79-44e54a63ab70.13.9.0"),sQuery(id+"F0.wireOp",EDGE,"4a86b1cf-17ad-482d-8b79-44e54a63ab70.13.10.0"),sQuery(id+"F0.wireOp",EDGE,"4a86b1cf-17ad-482d-8b79-44e54a63ab70.13.11.0"),sQuery(id+"F0.wireOp",EDGE,"4a86b1cf-17ad-482d-8b79-44e54a63ab70.14.1.0"),sQuery(id+"F0.wireOp",EDGE,"4a86b1cf-17ad-482d-8b79-44e54a63ab70.14.2.0"),sQuery(id+"F0.wireOp",EDGE,"4a86b1cf-17ad-482d-8b79-44e54a63ab70.14.3.0"),sQuery(id+"F0.wireOp",EDGE,"4a86b1cf-17ad-482d-8b79-44e54a63ab70.14.4.0"),sQuery(id+"F0.wireOp",EDGE,"4a86b1cf-17ad-482d-8b79-44e54a63ab70.14.5.0"),sQuery(id+"F0.wireOp",EDGE,"4a86b1cf-17ad-482d-8b79-44e54a63ab70.14.6.0"),sQuery(id+"F0.wireOp",EDGE,"4a86b1cf-17ad-482d-8b79-44e54a63ab70.14.7.0"),sQuery(id+"F0.wireOp",EDGE,"4a86b1cf-17ad-482d-8b79-44e54a63ab70.14.8.0"),sQuery(id+"F0.wireOp",EDGE,"4a86b1cf-17ad-482d-8b79-44e54a63ab70.14.9.0"),sQuery(id+"F0.wireOp",EDGE,"4a86b1cf-17ad-482d-8b79-44e54a63ab70.14.10.0"),sQuery(id+"F0.wireOp",EDGE,"4a86b1cf-17ad-482d-8b79-44e54a63ab70.14.11.0"),sQuery(id+"F2.wireOp",EDGE,"E5.bottom"),sQuery(id+"F2.wireOp",EDGE,"E5.top"),sQuery(id+"F2.wireOp",EDGE,"E5.left"),sQuery(id+"F2.wireOp",EDGE,"E5.right"),sQuery(id+"F2.wireOp",EDGE,"E6.filletArc"),sQuery(id+"F2.wireOp",EDGE,"E7.filletArc"),sQuery(id+"F2.wireOp",EDGE,"E8.filletArc"),sQuery(id+"F2.wireOp",EDGE,"E9.filletArc")])],"isStart":false})});
            var sketch = newSketch(context, id + "F4", { "sketchPlane" : qUnion([Q0])});
            skLineSegment(sketch, "E10.bottom", {"start": v(149.22, -110.49) * mm, "end": v(-149.23, -110.5) * mm});
            skLineSegment(sketch, "E10.top", {"start": v(149.23, 110.5) * mm, "end": v(-149.23, 110.49) * mm});
            skLineSegment(sketch, "E10.left", {"start": v(149.23, -110.49) * mm, "end": v(149.23, 110.5) * mm});
            skLineSegment(sketch, "E10.right", {"start": v(-149.23, -110.5) * mm, "end": v(-149.23, 110.49) * mm});
            skPoint(sketch, "E10.middle", {"position": v(0, 0) * mm});
            skSolve(sketch);
        }
        {
            var Q0;
            Q0=makeQuery(id+"F4.imprint","IMPRINT",FACE,{"disambiguationData":[TD([[makeQuery(id+"F4.imprint","IMPRINT",EDGE,{"derivedFrom":sQuery(id+"F4.wireOp",EDGE,"E10.bottom")}),-1.0]])]});
            extrude(context, id + "F5", {"entities" : qUnion([Q0]), "operationType" : NewBodyOperationType.REMOVE, "oppositeDirection" : true, "depth" : 25.4 * mm, "offsetDistance" : 25.4 * mm});
        }
    });
